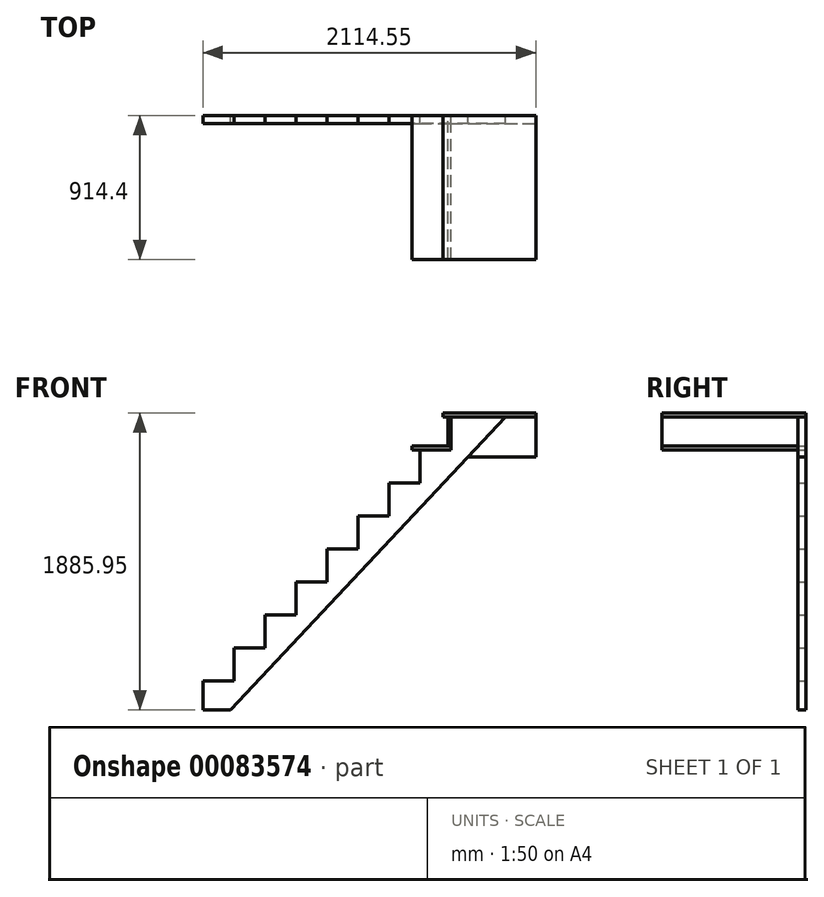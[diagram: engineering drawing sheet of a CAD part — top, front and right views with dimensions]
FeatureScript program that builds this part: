
annotation { "Feature Type Name" : "Feature", "Feature Type Description" : "" }
export const myFeature = defineFeature(function(context is Context, id is Id, definition is map)
    precondition{}
    {
        {
            var Q0;
            Q0=qCreatedBy(makeId("Front.planeOp"),FACE);
            var sketch = newSketch(context, id + "F0", { "sketchPlane" : qUnion([Q0])});
            skLineSegment(sketch, "E0", {"start": v(0, 0) * mm, "end": v(2133.6, 0) * mm});
            skLineSegment(sketch, "E1", {"start": v(2133.6, 0) * mm, "end": v(2133.6, 1981.2) * mm});
            skLineSegment(sketch, "E2", {"start": v(0, 0) * mm, "end": v(0, 209.55) * mm});
            skLineSegment(sketch, "E3", {"start": v(-31.75, 209.55) * mm, "end": v(196.85, 209.55) * mm});
            skLineSegment(sketch, "E4", {"start": v(196.85, 209.55) * mm, "end": v(196.85, 419.1) * mm});
            skLineSegment(sketch, "E5", {"start": v(165.1, 419.1) * mm, "end": v(393.7, 419.1) * mm});
            skLineSegment(sketch, "E6", {"start": v(393.7, 419.1) * mm, "end": v(393.7, 628.65) * mm});
            skLineSegment(sketch, "E7", {"start": v(361.95, 628.65) * mm, "end": v(590.55, 628.65) * mm});
            skLineSegment(sketch, "E8", {"start": v(590.55, 628.65) * mm, "end": v(590.55, 838.2) * mm});
            skLineSegment(sketch, "E9", {"start": v(558.8, 838.2) * mm, "end": v(787.4, 838.2) * mm});
            skLineSegment(sketch, "E10", {"start": v(787.4, 838.2) * mm, "end": v(787.4, 1047.75) * mm});
            skLineSegment(sketch, "E11", {"start": v(755.65, 1047.75) * mm, "end": v(984.25, 1047.75) * mm});
            skLineSegment(sketch, "E12", {"start": v(984.25, 1047.75) * mm, "end": v(984.25, 1257.3) * mm});
            skLineSegment(sketch, "E13", {"start": v(952.5, 1257.3) * mm, "end": v(1181.1, 1257.3) * mm});
            skLineSegment(sketch, "E14", {"start": v(1181.1, 1257.3) * mm, "end": v(1181.1, 1466.85) * mm});
            skLineSegment(sketch, "E15", {"start": v(1149.35, 1466.85) * mm, "end": v(1377.95, 1466.85) * mm});
            skLineSegment(sketch, "E16", {"start": v(1377.95, 1466.85) * mm, "end": v(1377.95, 1676.4) * mm});
            skLineSegment(sketch, "E17", {"start": v(1346.2, 1676.4) * mm, "end": v(1574.8, 1676.4) * mm});
            skLineSegment(sketch, "E18", {"start": v(1574.8, 1676.4) * mm, "end": v(1574.8, 1885.95) * mm});
            skLineSegment(sketch, "E19", {"start": v(1543.05, 1885.95) * mm, "end": v(2133.6, 1885.95) * mm});
            skLineSegment(sketch, "E20", {"start": v(1747.79, 1860.55) * mm, "end": v(0, 0) * mm, "construction": true});
            skLineSegment(sketch, "E21", {"start": v(1543.05, 1885.95) * mm, "end": v(1543.05, 1860.55) * mm});
            skLineSegment(sketch, "E22", {"start": v(1543.05, 1860.55) * mm, "end": v(2133.6, 1860.55) * mm});
            skLineSegment(sketch, "E23", {"start": v(1574.8, 1676.4) * mm, "end": v(1593.85, 1676.4) * mm});
            skLineSegment(sketch, "E24", {"start": v(1593.85, 1676.4) * mm, "end": v(1593.85, 1860.55) * mm});
            skLineSegment(sketch, "E25", {"start": v(1346.2, 1676.4) * mm, "end": v(1346.2, 1651) * mm});
            skLineSegment(sketch, "E26", {"start": v(1377.95, 1466.85) * mm, "end": v(1397, 1466.85) * mm});
            skLineSegment(sketch, "E27", {"start": v(1397, 1466.85) * mm, "end": v(1397, 1651) * mm});
            skLineSegment(sketch, "E28", {"start": v(1942.35, 1860.55) * mm, "end": v(194.56, 0) * mm});
            skLineSegment(sketch, "E29", {"start": v(1346.2, 1651) * mm, "end": v(1593.85, 1651) * mm});
            skLineSegment(sketch, "E30", {"start": v(1593.85, 1651) * mm, "end": v(1593.85, 1676.4) * mm});
            skLineSegment(sketch, "E31", {"start": v(1149.35, 1466.85) * mm, "end": v(1149.35, 1441.45) * mm});
            skLineSegment(sketch, "E32", {"start": v(1149.35, 1441.45) * mm, "end": v(1397, 1441.45) * mm});
            skLineSegment(sketch, "E33", {"start": v(1397, 1441.45) * mm, "end": v(1397, 1466.85) * mm});
            skLineSegment(sketch, "E34", {"start": v(1200.15, 1441.45) * mm, "end": v(1200.15, 1257.3) * mm});
            skLineSegment(sketch, "E35", {"start": v(1200.15, 1257.3) * mm, "end": v(1181.1, 1257.3) * mm});
            skLineSegment(sketch, "E36", {"start": v(952.5, 1257.3) * mm, "end": v(952.5, 1231.9) * mm});
            skLineSegment(sketch, "E37", {"start": v(952.5, 1231.9) * mm, "end": v(1200.15, 1231.9) * mm});
            skLineSegment(sketch, "E38", {"start": v(1200.15, 1231.9) * mm, "end": v(1200.15, 1257.3) * mm});
            skLineSegment(sketch, "E39", {"start": v(1003.3, 1231.9) * mm, "end": v(1003.3, 1047.75) * mm});
            skLineSegment(sketch, "E40", {"start": v(1003.3, 1047.75) * mm, "end": v(984.25, 1047.75) * mm});
            skLineSegment(sketch, "E41", {"start": v(755.65, 1047.75) * mm, "end": v(755.65, 1022.35) * mm});
            skLineSegment(sketch, "E42", {"start": v(755.65, 1022.35) * mm, "end": v(1003.3, 1022.35) * mm});
            skLineSegment(sketch, "E43", {"start": v(1003.3, 1022.35) * mm, "end": v(1003.3, 1047.75) * mm});
            skLineSegment(sketch, "E44", {"start": v(806.45, 1022.35) * mm, "end": v(806.45, 838.2) * mm});
            skLineSegment(sketch, "E45", {"start": v(806.45, 838.2) * mm, "end": v(787.4, 838.2) * mm});
            skLineSegment(sketch, "E46", {"start": v(558.8, 838.2) * mm, "end": v(558.8, 812.8) * mm});
            skLineSegment(sketch, "E47", {"start": v(558.8, 812.8) * mm, "end": v(806.45, 812.8) * mm});
            skLineSegment(sketch, "E48", {"start": v(806.45, 812.8) * mm, "end": v(806.45, 838.2) * mm});
            skLineSegment(sketch, "E49", {"start": v(609.6, 812.8) * mm, "end": v(609.6, 628.65) * mm});
            skLineSegment(sketch, "E50", {"start": v(609.6, 628.65) * mm, "end": v(590.55, 628.65) * mm});
            skLineSegment(sketch, "E51", {"start": v(361.95, 628.65) * mm, "end": v(361.95, 603.25) * mm});
            skLineSegment(sketch, "E52", {"start": v(361.95, 603.25) * mm, "end": v(609.6, 603.25) * mm});
            skLineSegment(sketch, "E53", {"start": v(609.6, 603.25) * mm, "end": v(609.6, 628.65) * mm});
            skLineSegment(sketch, "E54", {"start": v(412.75, 603.25) * mm, "end": v(412.75, 419.1) * mm});
            skLineSegment(sketch, "E55", {"start": v(412.75, 419.1) * mm, "end": v(393.7, 419.1) * mm});
            skLineSegment(sketch, "E56", {"start": v(165.1, 419.1) * mm, "end": v(165.1, 393.7) * mm});
            skLineSegment(sketch, "E57", {"start": v(165.1, 393.7) * mm, "end": v(412.75, 393.7) * mm});
            skLineSegment(sketch, "E58", {"start": v(412.75, 393.7) * mm, "end": v(412.75, 419.1) * mm});
            skLineSegment(sketch, "E59", {"start": v(215.9, 393.7) * mm, "end": v(215.9, 209.55) * mm});
            skLineSegment(sketch, "E60", {"start": v(215.9, 209.55) * mm, "end": v(196.85, 209.55) * mm});
            skLineSegment(sketch, "E61", {"start": v(-31.75, 209.55) * mm, "end": v(-31.75, 184.15) * mm});
            skLineSegment(sketch, "E62", {"start": v(-31.75, 184.15) * mm, "end": v(215.9, 184.15) * mm});
            skLineSegment(sketch, "E63", {"start": v(215.9, 184.15) * mm, "end": v(215.9, 209.55) * mm});
            skLineSegment(sketch, "E64", {"start": v(19.05, 184.15) * mm, "end": v(19.05, 0) * mm});
            skLineSegment(sketch, "E65", {"start": v(1703.74, 1606.55) * mm, "end": v(2133.6, 1606.55) * mm});
            skSolve(sketch);
        }
        {
            var Q0;
            {var subQ18=sQuery(id+"F0.wireOp",EDGE,"E24");Q0=makeQuery(id+"F0.imprint","IMPRINT",FACE,{"disambiguationData":[TD([[makeQuery(id+"F0.imprint","IMPRINT",EDGE,{"derivedFrom":subQ18}),-1.0]])]});}
            extrude(context, id + "F1", {"entities" : qUnion([Q0]), "depth" : 50.8 * mm});
        }
        {
            var Q0;
            {var subQ4=sQuery(id+"F0.wireOp",EDGE,"E23");Q0=makeQuery(id+"F0.imprint","IMPRINT",FACE,{"disambiguationData":[TD([[makeQuery(id+"F0.imprint","IMPRINT",EDGE,{"derivedFrom":subQ4}),-1.0]])]});}
            var Q1;
            {var subQ5=sQuery(id+"F0.wireOp",EDGE,"E25");Q1=makeQuery(id+"F0.imprint","IMPRINT",FACE,{"disambiguationData":[TD([[makeQuery(id+"F0.imprint","IMPRINT",EDGE,{"derivedFrom":subQ5}),1.0]])]});}
            extrude(context, id + "F2", {"entities" : qUnion([Q0, Q1]), "depth" : 914.4 * mm});
        }
        {
            var Q0;
            {var subQ4=sQuery(id+"F0.wireOp",EDGE,"E19");var subQ6=sQuery(id+"F0.wireOp",EDGE,"E1");var subQ7=makeQuery(id+"F0.imprint","INTERSECT",VERTEX,{"derivedFrom":[subQ6,subQ4]});Q0=makeQuery(id+"F0.imprint","IMPRINT",FACE,{"disambiguationData":[TD([[makeQuery(id+"F0.imprint","IMPRINT",EDGE,{"disambiguationData":[TD([[subQ7,1.0]])],"derivedFrom":subQ6}),1.0]])]});}
            var Q1;
            {var subQ5=sQuery(id+"F0.wireOp",EDGE,"E21");Q1=makeQuery(id+"F0.imprint","IMPRINT",FACE,{"disambiguationData":[TD([[makeQuery(id+"F0.imprint","IMPRINT",EDGE,{"derivedFrom":subQ5}),1.0]])]});}
            extrude(context, id + "F3", {"entities" : qUnion([Q0, Q1]), "depth" : 914.4 * mm});
        }
        {
            var Q0;
            {var subQ0=sQuery(id+"F0.wireOp",EDGE,"E23");Q0=makeQuery(id+"F0.imprint","IMPRINT",FACE,{"disambiguationData":[TD([[makeQuery(id+"F0.imprint","IMPRINT",EDGE,{"derivedFrom":subQ0}),1.0]])]});}
            extrude(context, id + "F4", {"entities" : qUnion([Q0]), "depth" : 914.4 * mm});
        }
        {
            var Q0;
            {var subQ3=sQuery(id+"F0.wireOp",EDGE,"E65");Q0=makeQuery(id+"F0.imprint","IMPRINT",FACE,{"disambiguationData":[TD([[makeQuery(id+"F0.imprint","IMPRINT",EDGE,{"derivedFrom":subQ3}),1.0]])]});}
            extrude(context, id + "F5", {"entities" : qUnion([Q0]), "depth" : 50.8 * mm});
        }
    });
